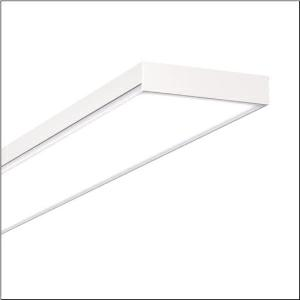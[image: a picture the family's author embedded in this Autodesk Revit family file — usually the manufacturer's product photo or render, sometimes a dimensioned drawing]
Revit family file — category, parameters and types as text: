
# Revit family: apollon_r__31_surface_51mp26wd2441wa_9052
name_source: partatom
category: Lighting Fixtures
units: mm (PartAtom-declared; Revit-internal decimal feet)

## family parameters
Cut with Voids When Loaded = No
Host = Face
Light Source = No
Part Type = Normal
Room Calculation Point = No
Round Connector Dimension = Use Diameter
Shared = No

## types (1)
- Apollon® 31 Surface (1 x LED, 4600 lm, 33 W, 4000K)
    Apparent Load = 33 VA
    CIE Flux Codes = 61 87 97 97 100
    Color Rendering = 80
    Color Temperature = 4000K
    Default Elevation = 1800 mm
    Description = Apollon® 31 Surface, office luminaire, primary optical cover: micro prismatic cover, of PMMA, light emission: direct distribution, primary light characteristic: symmetric, installation type: surface-mounted, LED, rated luminous flux: 4.600lm, luminous efficacy: 139lm/W, light colour: 840, colour temperature: 4000K, control gear: ECG DALI, with terminal, 5-pole, mains connection: 220..240V, AC, 50/60Hz, rated input power: 33W, housing, of sheet steel, coil coated, traffic white (RAL 9016), length: 1.545mm, width: 200mm, height: 44mm, protection rating (complete): IP20, insulation class (complete): insulation class II (safety insulation), certification: CE, impact resistance: IK02, permissible operating ambient temperature: -20..+40°C, standard: EN 60598-2-22, packaging unit: 1 piece
    Height = 44 mm
    Lamp = 1 x LED
    Lamp Light Flux = 4600 lm
    Lamp Power = 33 W
    Lamp count = 1
    Length = 1545 mm
    Luminous efficacy = 139 lm/W
    Manufacturer = Siteco
    ModVariant = No
    Model = 51MP26WD2441WA
    Mounting Place = Ceiling
    Mounting Type = Surface mounted
    Number of Poles = 1
    OnlyDefault = Yes
    Power Factor = 1
    Product Name = Apollon® 31 Surface
    Product group = office luminaire | ceiling mounted
    ProductGroupID = 300
    Protection Class = Protection class II
    Protection Degree = IP 20
    RLX_Detail_Level = 1
    RLX_Emergency_Light_Flux = 0 lm
    RLX_Emergency_Type = 0
    RLX_Emergency_Type_DB = No
    RlxData = <blob elided: 20773 chars, md5=7e50dd5c>
    Socket = socket
    Standby Power = 0 W
    System Light Flux = 4600 lm
    System Power = 33 W
    Type Comments = Product without accessories
    Type Image = l_1313658.jpg
    URL = http://relux.com
    VarID = ---
    Voltage = 0 V
    Weight = 0.00 kg
    Width = 200 mm  [stored 0.656168 ft]

note: [stored X ft] marks values corroborated as IEEE doubles in the binary element streams (Revit-internal decimal feet)

## geometry (parser evidence)
native form markers: Blend x4, Sweep x9
no freeform markers — native parametric forms only
